# Revit family: Haworth_XSeries_LateralFile_21h
name_source: partatom
category: Furniture Systems
revit_build: Autodesk Revit 2018 (Build: 20170223_1515(x64)
units: mm (PartAtom-declared; Revit-internal decimal feet)

## family parameters
Always vertical = Yes
Cut with Voids When Loaded = No
OmniClass Number = 23.40.70.14.64.21
OmniClass Title = Systems Furniture
Part Type = Normal
Room Calculation Point = No
Round Connector Dimension = Use Diameter
Shared = No
Work Plane-Based = No

## types (1)
- 18d 36w 21h - Proud Style
    # of Drawers = 2
    Actual # of Drawers = 2
    Actual Depth = 18 3/4"
    Actual Height = 21 1/2"
    Actual Width = 35 7/8"
    Assembly Code = E2020200
    Cabinet Height = 21 1/2"
    Crescent Pull = No
    Custom Size = No
    Description = Haworth XSeries Lateral File - 18d 36w 21h - Proud Style
    Drawer 3 = No
    Drawer 4 = No
    Drawer Height = 12 3/16"
    Drawer Width = 35 7/8"
    Ellipse Pull = No
    Inset Style = No
    Integral Pull = No
    J Pull = Yes
    Linear Pull = No
    Manufacturer = Haworth
    Max # of Drawers = 5
    Max. Height = 63 1/2"
    Max. Width = 47 7/8"
    Min. Height = 27 1/2"
    Min. Width = 29 7/8"
    Model = JLPD
    Not Open = Yes
    Open = No
    Proud Offset = 3/4"
    Proud Style = Yes
    Pull Classic = No
    Pull Finish = Haworth _ Paint _ Smoke
    Radius Pull = No
    Revision Number = 2
    Second Drawer Height = 6"
    Size = Verify Final Dim. w/ Haworth
    Standard Widths = 30, 36, 42 in.
    Sustainability Info = https://www.haworth.com
    Taper Pull = No
    URL = http://www.haworth.com
    URL - Product = https://www.haworth.com
    Warranty = http://www.haworth.com
    Width = 36"

## geometry (parser evidence)
native form markers: Sweep x6
no freeform markers — native parametric forms only
